# Revit family: Steel-HST Purlin-Steel & Tube-G450A
name_source: partatom
category: Structural Framing
revit_build: Autodesk Revit 2016 (Build: 20160314_0715(x64)
units: mm (PartAtom-declared; Revit-internal decimal feet)

## family parameters
Always export as geometry = No
Always vertical = Yes
Cut with Voids When Loaded = No
Material for Model Behavior = Steel
OmniClass Number = 23.25.30.11.14.14
OmniClass Title = Beams
Section Shape = C Profile with Fold
Shared = No
Show family pre-cut in plan views = Yes
Structural Framing Length Roundoff = 0 mm

## types (1)
- HST400/30
    Assembly Code = B1020230
    CBICode = 3411
    CBIDescription = Structural steelwork
    Centroid Horizontal = 28.3 mm
    Centroid Vertical = 200.0 mm
    Coil Performance = Gauge 1.15-1.45mm; G500(MPa); 275g/m² (Zinc): Gauge 1.75-3.0mm; G450 (MPa); 275g/m²(Zinc)
    Description = HST Steel Purlins and Girts are high strength lipped profile sections, providing an economic solution for your building project.
    Design Instruction = All the design information should be cross referenced with the current Steel & Tube Purlins and Girts design guide, and AS/NZS 4600:2005
    Design Standard = Steel & Tube’s HST purlins and Girts profiles are designed in accordance with AS/NZS 4600:2005.
    Elastic Modulus strong axis = 234000.0 mm³
    Elastic Modulus weak axis = 42500.0 mm³
    Fold Length = 12.0 mm
    Height = 400.0 mm
    Inner Fillet = 5.0 mm
    Lip Length = 48.0 mm
    Manufacturer = Steel & Tube
    ManufacturerName = Steel & Tube
    ManufacturerURL = http://www.steelandtube.co.nz
    MassPerUnitLength_ANZRS = 16.48 kg/m
    Material Standard = Steel & Tube’s HST purlins and Girts profiles are manufactured from materials conforming to AS1397:2011
    Model = HST400/30
    ModifiedIssue_ANZRS = 20160330 $
    Moment of Inertia strong axis = 46900000.00 mm4
    Moment of Inertia weak axis = 2920000.00 mm4
    Nominal Weight = 16.48 kgf/m
    Perimeter = 0.00 m²/m
    Plastic Modulus strong axis = 234000.0 mm³
    Plastic Modulus weak axis = 42500.0 mm³
    Principal Axes Angle = 0.00°
    Profile1 = No
    Profile2 = No
    Profile2 Height Validation = 152 mm  [stored 0.498688 ft]
    Profile23Medium = Yes
    Profile3 = Yes
    Profile3 Height Validation = 400 mm  [stored 1.31234 ft]
    Section Area = 2071.0 mm²
    SectionAreaGross_ANZRS = 2071.0 mm²
    SectionAreaNet_ANZRS = 2071.0 mm²
    Shear Area strong axis = 2071.0 mm²
    Shear Area weak axis = 2071.0 mm²
    SpecificationDescription = Steel & Tube Purlins & Girts
    SpecificationReference = 3411ST
    Structural Material = Metal-Steel-450MPa
    Torsional Modulus = 0.0 mm³
    Torsional Moment of Inertia = 6214.00 mm4
    Type Comments = HST Steel Purlins and Girts
    URL = http://www.steelandtube.co.nz
    Uniclass2015Code = Pr_20_76_51_21
    Uniclass2015Title = Cold-formed galvanized steel sections
    Uniclass2015Version = 2015
    Wall Design Thickness = 3.0 mm
    Wall Nominal Thickness = 3.0 mm
    Warping Constant = 106000000000.0 mm6
    Width = 100.0 mm
    b1 = 10.0 mm
    d1 = 75.0 mm
    d2 = 132.0 mm
    d3 = 25.0 mm
    d4 = 191.0 mm

note: [stored X ft] marks values corroborated as IEEE doubles in the binary element streams (Revit-internal decimal feet)

## geometry (parser evidence)
native form markers: Sweep x6
no freeform markers — native parametric forms only
